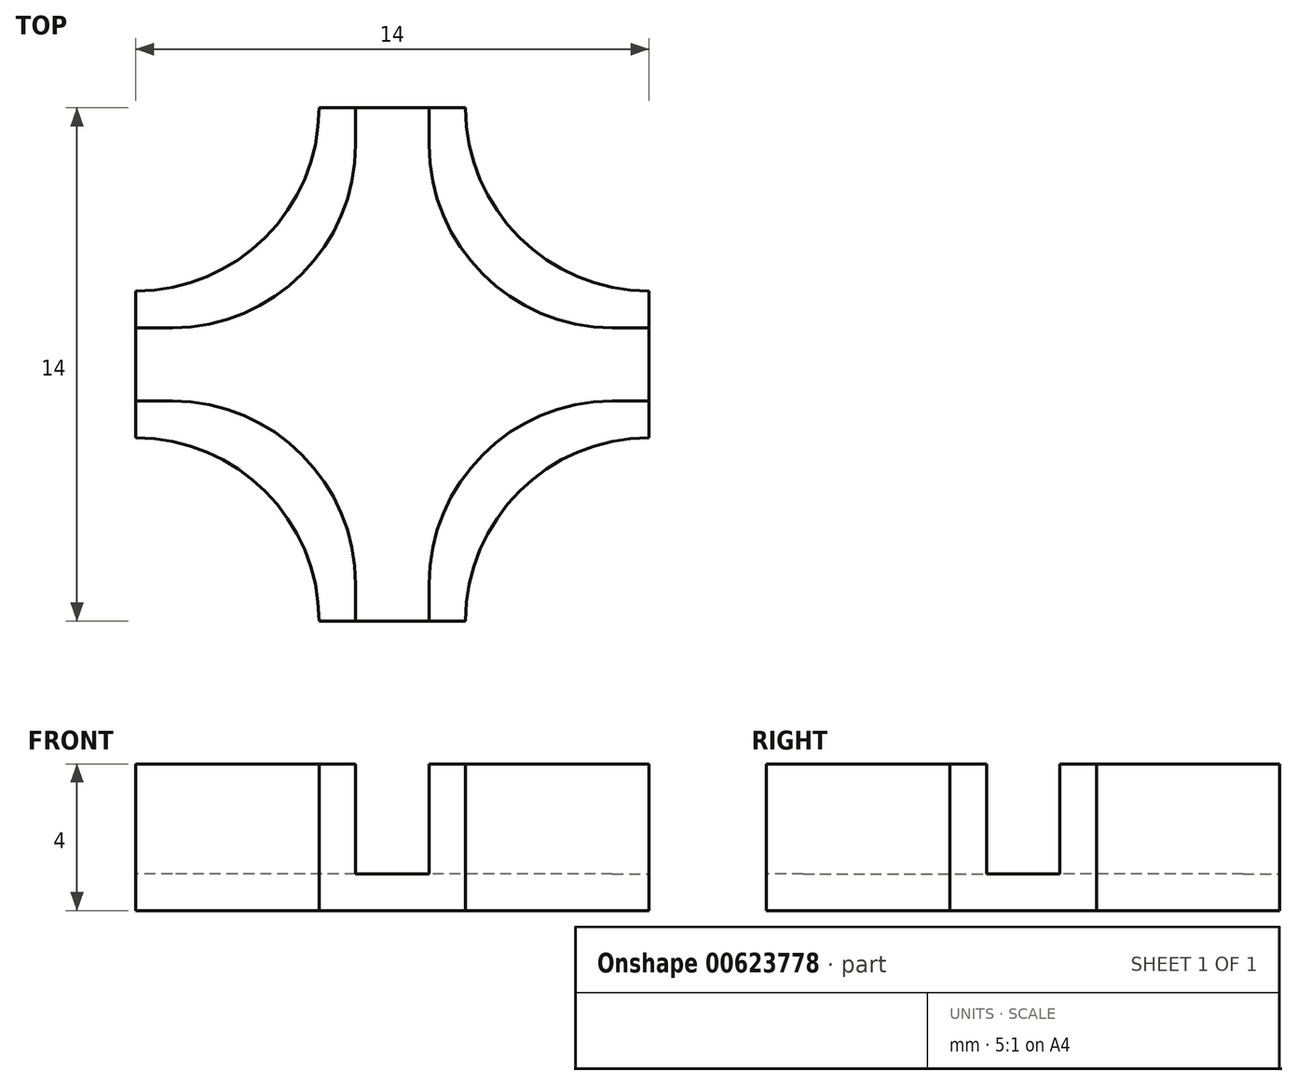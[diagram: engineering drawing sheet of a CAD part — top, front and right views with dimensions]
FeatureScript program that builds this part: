
annotation { "Feature Type Name" : "Feature", "Feature Type Description" : "" }
export const myFeature = defineFeature(function(context is Context, id is Id, definition is map)
    precondition{}
    {
        {
            var Q0;
            Q0=qCreatedBy(makeId("Top.planeOp"),FACE);
            var sketch = newSketch(context, id + "F0", { "sketchPlane" : qUnion([Q0])});
            skLineSegment(sketch, "E0.bottom", {"start": v(7, -7) * mm, "end": v(-7, -7) * mm});
            skLineSegment(sketch, "E0.top", {"start": v(7, 7) * mm, "end": v(-7, 7) * mm});
            skLineSegment(sketch, "E0.left", {"start": v(7, -7) * mm, "end": v(7, 7) * mm});
            skLineSegment(sketch, "E0.right", {"start": v(-7, -7) * mm, "end": v(-7, 7) * mm});
            skPoint(sketch, "E0.middle", {"position": v(0, 0) * mm});
            skSolve(sketch);
        }
        {
            var Q0;
            Q0=makeQuery(id+"F0.imprint","IMPRINT",FACE,{"disambiguationData":[TD([[makeQuery(id+"F0.imprint","IMPRINT",EDGE,{"derivedFrom":sQuery(id+"F0.wireOp",EDGE,"E0.bottom")}),-1.0]])]});
            extrude(context, id + "F1", {"entities" : qUnion([Q0]), "depth" : 1 * mm, "offsetDistance" : 25 * mm});
        }
        {
            var Q0;
            Q0=makeQuery(id+"F1.opExtrude","CAP_FACE",FACE,{"disambiguationData":[OSD([sQuery(id+"F0.wireOp",EDGE,"E0.bottom"),sQuery(id+"F0.wireOp",EDGE,"E0.top"),sQuery(id+"F0.wireOp",EDGE,"E0.left"),sQuery(id+"F0.wireOp",EDGE,"E0.right")])],"isStart":false});
            var sketch = newSketch(context, id + "F2", { "sketchPlane" : qUnion([Q0])});
            skLineSegment(sketch, "E1", {"start": v(-1, 7) * mm, "end": v(-1, -7) * mm, "construction": true});
            skLineSegment(sketch, "E2", {"start": v(1, 7) * mm, "end": v(1, -7) * mm, "construction": true});
            skLineSegment(sketch, "E3", {"start": v(0, 5.56) * mm, "end": v(1, 5.56) * mm, "construction": true});
            skLineSegment(sketch, "E4", {"start": v(0, 5.56) * mm, "end": v(-1, 5.56) * mm, "construction": true});
            skLineSegment(sketch, "E5", {"start": v(-7, 1) * mm, "end": v(7, 1) * mm, "construction": true});
            skLineSegment(sketch, "E6", {"start": v(-7, -1) * mm, "end": v(7, -1) * mm, "construction": true});
            skLineSegment(sketch, "E7", {"start": v(-4.1, 0) * mm, "end": v(-4.1, -1) * mm, "construction": true});
            skLineSegment(sketch, "E8", {"start": v(-4.57, 1) * mm, "end": v(-4.57, 0) * mm, "construction": true});
            skLineSegment(sketch, "E9.bottom", {"start": v(1, -1) * mm, "end": v(2, -1) * mm});
            skLineSegment(sketch, "E9.top", {"start": v(1, -7) * mm, "end": v(2, -7) * mm});
            skLineSegment(sketch, "E9.left", {"start": v(1, -1) * mm, "end": v(1, -7) * mm});
            skLineSegment(sketch, "E9.right", {"start": v(2, -1) * mm, "end": v(2, -7) * mm});
            skLineSegment(sketch, "E10.bottom", {"start": v(1, 1) * mm, "end": v(2, 1) * mm});
            skLineSegment(sketch, "E10.top", {"start": v(1, 7) * mm, "end": v(2, 7) * mm});
            skLineSegment(sketch, "E10.left", {"start": v(1, 1) * mm, "end": v(1, 7) * mm});
            skLineSegment(sketch, "E10.right", {"start": v(2, 1) * mm, "end": v(2, 7) * mm});
            skLineSegment(sketch, "E11.bottom", {"start": v(-1, 1) * mm, "end": v(-2, 1) * mm});
            skLineSegment(sketch, "E11.top", {"start": v(-1, 7) * mm, "end": v(-2, 7) * mm});
            skLineSegment(sketch, "E11.left", {"start": v(-1, 1) * mm, "end": v(-1, 7) * mm});
            skLineSegment(sketch, "E11.right", {"start": v(-2, 1) * mm, "end": v(-2, 7) * mm});
            skLineSegment(sketch, "E12.bottom", {"start": v(-1, -1) * mm, "end": v(-2, -1) * mm});
            skLineSegment(sketch, "E12.top", {"start": v(-1, -7) * mm, "end": v(-2, -7) * mm});
            skLineSegment(sketch, "E12.left", {"start": v(-1, -1) * mm, "end": v(-1, -7) * mm});
            skLineSegment(sketch, "E12.right", {"start": v(-2, -1) * mm, "end": v(-2, -7) * mm});
            skLineSegment(sketch, "E13.bottom", {"start": v(2, -1) * mm, "end": v(7, -1) * mm});
            skLineSegment(sketch, "E13.top", {"start": v(2, -2) * mm, "end": v(7, -2) * mm});
            skLineSegment(sketch, "E13.left", {"start": v(2, -1) * mm, "end": v(2, -2) * mm});
            skLineSegment(sketch, "E13.right", {"start": v(7, -1) * mm, "end": v(7, -2) * mm});
            skLineSegment(sketch, "E14.bottom", {"start": v(-2, -1) * mm, "end": v(-7, -1) * mm});
            skLineSegment(sketch, "E14.top", {"start": v(-2, -2) * mm, "end": v(-7, -2) * mm});
            skLineSegment(sketch, "E14.left", {"start": v(-2, -1) * mm, "end": v(-2, -2) * mm});
            skLineSegment(sketch, "E14.right", {"start": v(-7, -1) * mm, "end": v(-7, -2) * mm});
            skLineSegment(sketch, "E15.bottom", {"start": v(-2, 1) * mm, "end": v(-7, 1) * mm});
            skLineSegment(sketch, "E15.top", {"start": v(-2, 2) * mm, "end": v(-7, 2) * mm});
            skLineSegment(sketch, "E15.left", {"start": v(-2, 1) * mm, "end": v(-2, 2) * mm});
            skLineSegment(sketch, "E15.right", {"start": v(-7, 1) * mm, "end": v(-7, 2) * mm});
            skLineSegment(sketch, "E16.bottom", {"start": v(2, 1) * mm, "end": v(7, 1) * mm});
            skLineSegment(sketch, "E16.top", {"start": v(2, 2) * mm, "end": v(7, 2) * mm});
            skLineSegment(sketch, "E16.left", {"start": v(2, 1) * mm, "end": v(2, 2) * mm});
            skLineSegment(sketch, "E16.right", {"start": v(7, 1) * mm, "end": v(7, 2) * mm});
            skSolve(sketch);
        }
        {
            var Q0;
            Q0=makeQuery(id+"F2.imprint","IMPRINT",FACE,{"disambiguationData":[TD([[makeQuery(id+"F2.imprint","IMPRINT",EDGE,{"derivedFrom":sQuery(id+"F2.wireOp",EDGE,"E11.bottom")}),-1.0]])]});
            var Q1;
            Q1=makeQuery(id+"F2.imprint","IMPRINT",FACE,{"disambiguationData":[TD([[makeQuery(id+"F2.imprint","IMPRINT",EDGE,{"derivedFrom":sQuery(id+"F2.wireOp",EDGE,"E15.bottom")}),-1.0]])]});
            var Q2;
            Q2=makeQuery(id+"F2.imprint","IMPRINT",FACE,{"disambiguationData":[TD([[makeQuery(id+"F2.imprint","IMPRINT",EDGE,{"derivedFrom":sQuery(id+"F2.wireOp",EDGE,"E10.bottom")}),1.0]])]});
            var Q3;
            Q3=makeQuery(id+"F2.imprint","IMPRINT",FACE,{"disambiguationData":[TD([[makeQuery(id+"F2.imprint","IMPRINT",EDGE,{"derivedFrom":sQuery(id+"F2.wireOp",EDGE,"E16.bottom")}),1.0]])]});
            var Q4;
            Q4=makeQuery(id+"F2.imprint","IMPRINT",FACE,{"disambiguationData":[TD([[makeQuery(id+"F2.imprint","IMPRINT",EDGE,{"derivedFrom":sQuery(id+"F2.wireOp",EDGE,"E13.bottom")}),-1.0]])]});
            var Q5;
            Q5=makeQuery(id+"F2.imprint","IMPRINT",FACE,{"disambiguationData":[TD([[makeQuery(id+"F2.imprint","IMPRINT",EDGE,{"derivedFrom":sQuery(id+"F2.wireOp",EDGE,"E9.bottom")}),-1.0]])]});
            var Q6;
            Q6=makeQuery(id+"F2.imprint","IMPRINT",FACE,{"disambiguationData":[TD([[makeQuery(id+"F2.imprint","IMPRINT",EDGE,{"derivedFrom":sQuery(id+"F2.wireOp",EDGE,"E14.bottom")}),1.0]])]});
            var Q7;
            Q7=makeQuery(id+"F2.imprint","IMPRINT",FACE,{"disambiguationData":[TD([[makeQuery(id+"F2.imprint","IMPRINT",EDGE,{"derivedFrom":sQuery(id+"F2.wireOp",EDGE,"E12.bottom")}),1.0]])]});
            extrude(context, id + "F3", {"entities" : qUnion([Q0, Q1, Q2, Q3, Q4, Q5, Q6, Q7]), "operationType" : NewBodyOperationType.ADD, "depth" : 3 * mm, "offsetDistance" : 25 * mm});
        }
        {
            var Q0;
            Q0=makeQuery(id+"F3.opExtrude","SWEPT_EDGE",EDGE,{"disambiguationData":[OSD([sQuery(id+"F2.wireOp",EDGE,"E9.right"),sQuery(id+"F2.wireOp",EDGE,"E13.top"),sQuery(id+"F2.wireOp",EDGE,"E13.left")])]});
            var Q1;
            Q1=makeQuery(id+"F3.opExtrude","SWEPT_EDGE",EDGE,{"disambiguationData":[OSD([sQuery(id+"F2.wireOp",EDGE,"E12.bottom"),sQuery(id+"F2.wireOp",EDGE,"E12.left")])]});
            var Q2;
            Q2=makeQuery(id+"F3.opExtrude","SWEPT_EDGE",EDGE,{"disambiguationData":[OSD([sQuery(id+"F2.wireOp",EDGE,"E11.bottom"),sQuery(id+"F2.wireOp",EDGE,"E11.left")])]});
            var Q3;
            Q3=makeQuery(id+"F3.opExtrude","SWEPT_EDGE",EDGE,{"disambiguationData":[OSD([sQuery(id+"F2.wireOp",EDGE,"E10.bottom"),sQuery(id+"F2.wireOp",EDGE,"E10.left")])]});
            var Q4;
            Q4=makeQuery(id+"F3.opExtrude","SWEPT_EDGE",EDGE,{"disambiguationData":[OSD([sQuery(id+"F2.wireOp",EDGE,"E10.right"),sQuery(id+"F2.wireOp",EDGE,"E16.top"),sQuery(id+"F2.wireOp",EDGE,"E16.left")])]});
            var Q5;
            Q5=makeQuery(id+"F3.opExtrude","SWEPT_EDGE",EDGE,{"disambiguationData":[OSD([sQuery(id+"F2.wireOp",EDGE,"E11.right"),sQuery(id+"F2.wireOp",EDGE,"E15.top"),sQuery(id+"F2.wireOp",EDGE,"E15.left")])]});
            var Q6;
            Q6=makeQuery(id+"F3.opExtrude","SWEPT_EDGE",EDGE,{"disambiguationData":[OSD([sQuery(id+"F2.wireOp",EDGE,"E12.right"),sQuery(id+"F2.wireOp",EDGE,"E14.top"),sQuery(id+"F2.wireOp",EDGE,"E14.left")])]});
            var Q7;
            Q7=makeQuery(id+"F3.opExtrude","SWEPT_EDGE",EDGE,{"disambiguationData":[OSD([sQuery(id+"F2.wireOp",EDGE,"E9.bottom"),sQuery(id+"F2.wireOp",EDGE,"E9.left")])]});
            fillet(context, id + "F4", {"entities" : qUnion([Q0, Q1, Q2, Q3, Q4, Q5, Q6, Q7]), "radius" : 5 * mm, "tangentPropagation" : true, "allowEdgeOverflow" : false});
        }
        {
            var Q0;
            {var subQ0=sQuery(id+"F0.wireOp",EDGE,"E0.left");var subQ1=sQuery(id+"F0.wireOp",EDGE,"E0.bottom");Q0=makeQuery(id+"F3.boolean.opBoolean","SPLIT",FACE,{"disambiguationData":[TD([makeQuery(id+"F3.opExtrude","SWEPT_FACE",FACE,{"disambiguationData":[OSD([sQuery(id+"F2.wireOp",EDGE,"E9.right")])]})])],"derivedFrom":makeQuery(id+"F1.opExtrude","CAP_FACE",FACE,{"disambiguationData":[OSD([subQ1,sQuery(id+"F0.wireOp",EDGE,"E0.top"),subQ0,sQuery(id+"F0.wireOp",EDGE,"E0.right")])],"isStart":false})});}
            var Q1;
            {var subQ0=sQuery(id+"F0.wireOp",EDGE,"E0.left");var subQ1=sQuery(id+"F0.wireOp",EDGE,"E0.top");Q1=makeQuery(id+"F3.boolean.opBoolean","SPLIT",FACE,{"disambiguationData":[TD([makeQuery(id+"F3.opExtrude","SWEPT_FACE",FACE,{"disambiguationData":[OSD([sQuery(id+"F2.wireOp",EDGE,"E10.right")])]})])],"derivedFrom":makeQuery(id+"F1.opExtrude","CAP_FACE",FACE,{"disambiguationData":[OSD([sQuery(id+"F0.wireOp",EDGE,"E0.bottom"),subQ1,subQ0,sQuery(id+"F0.wireOp",EDGE,"E0.right")])],"isStart":false})});}
            var Q2;
            {var subQ0=sQuery(id+"F0.wireOp",EDGE,"E0.right");var subQ1=sQuery(id+"F0.wireOp",EDGE,"E0.top");Q2=makeQuery(id+"F3.boolean.opBoolean","SPLIT",FACE,{"disambiguationData":[TD([makeQuery(id+"F3.opExtrude","SWEPT_FACE",FACE,{"disambiguationData":[OSD([sQuery(id+"F2.wireOp",EDGE,"E11.right")])]})])],"derivedFrom":makeQuery(id+"F1.opExtrude","CAP_FACE",FACE,{"disambiguationData":[OSD([sQuery(id+"F0.wireOp",EDGE,"E0.bottom"),subQ1,sQuery(id+"F0.wireOp",EDGE,"E0.left"),subQ0])],"isStart":false})});}
            var Q3;
            {var subQ0=sQuery(id+"F0.wireOp",EDGE,"E0.bottom");var subQ1=sQuery(id+"F0.wireOp",EDGE,"E0.right");Q3=makeQuery(id+"F3.boolean.opBoolean","SPLIT",FACE,{"disambiguationData":[TD([makeQuery(id+"F3.opExtrude","SWEPT_FACE",FACE,{"disambiguationData":[OSD([sQuery(id+"F2.wireOp",EDGE,"E12.right")])]})])],"derivedFrom":makeQuery(id+"F1.opExtrude","CAP_FACE",FACE,{"disambiguationData":[OSD([subQ0,sQuery(id+"F0.wireOp",EDGE,"E0.top"),sQuery(id+"F0.wireOp",EDGE,"E0.left"),subQ1])],"isStart":false})});}
            extrude(context, id + "F5", {"entities" : qUnion([Q0, Q1, Q2, Q3]), "operationType" : NewBodyOperationType.REMOVE, "oppositeDirection" : true, "depth" : 25 * mm, "offsetDistance" : 25 * mm});
        }
    });
